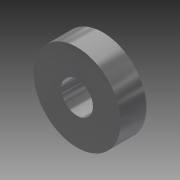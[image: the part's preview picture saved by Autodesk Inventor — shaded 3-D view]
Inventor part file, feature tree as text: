
AUTODESK INVENTOR PART (.ipt)
format: ipt  version: 2014 (Build 180170000, 170)  size: 83,968 bytes
history: native  units: in
note: dims shown in document units (in); Inventor stores cm internally (conversion verified against a paired STEP export)
features: plane x3, extrude x1, sketch x1
ambient origin geometry x8: Origin, YZ Plane, XZ Plane, XY Plane, X Axis, Y Axis, Z Axis, Center Point
bodies: Solid1 (feature_tree)
feature tree (5):
  extrude  "Extrusion1"  Depth=0.55in
  plane  "Work Plane1"
  plane  "Work Plane2"
  plane  "Work Plane3"
  sketch  "Sketch1"  dims[d0=1.85in d1=0.675in d2=0.55in d3=0.0in d4=0.0in d5=0.0in]
